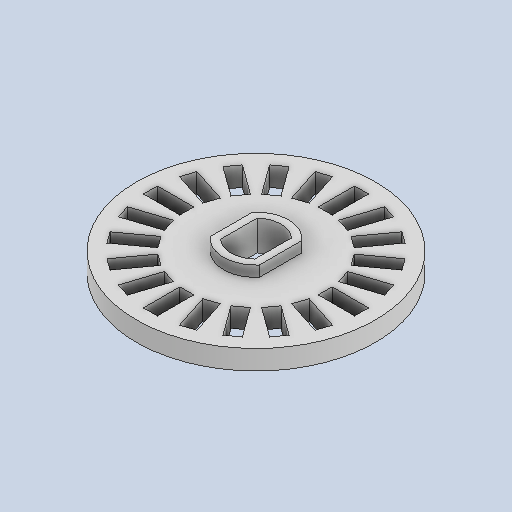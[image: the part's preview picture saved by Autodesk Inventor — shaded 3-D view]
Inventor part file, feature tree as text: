
AUTODESK INVENTOR PART (.ipt)
format: ipt  version: 2022 (Build 260153070, 153G)  size: 245,760 bytes
history: native  units: in
note: dims shown in document units (in); Inventor stores cm internally (conversion verified against a paired STEP export)
features: other x3, sketch x2
ambient origin geometry x8: Origin, YZ Plane, XZ Plane, XY Plane, X Axis, Y Axis, Z Axis, Center Point
bodies: Solid1 (feature_tree)
feature tree (5):
  other  "TT encoder disk.ipt"
  other  "Solid1::TT encoder disk.ipt"
  other  "TaggingFeature1"
  sketch  "Sketch1"  dims[d0=0.3937in]
  sketch  "Sketch2"
